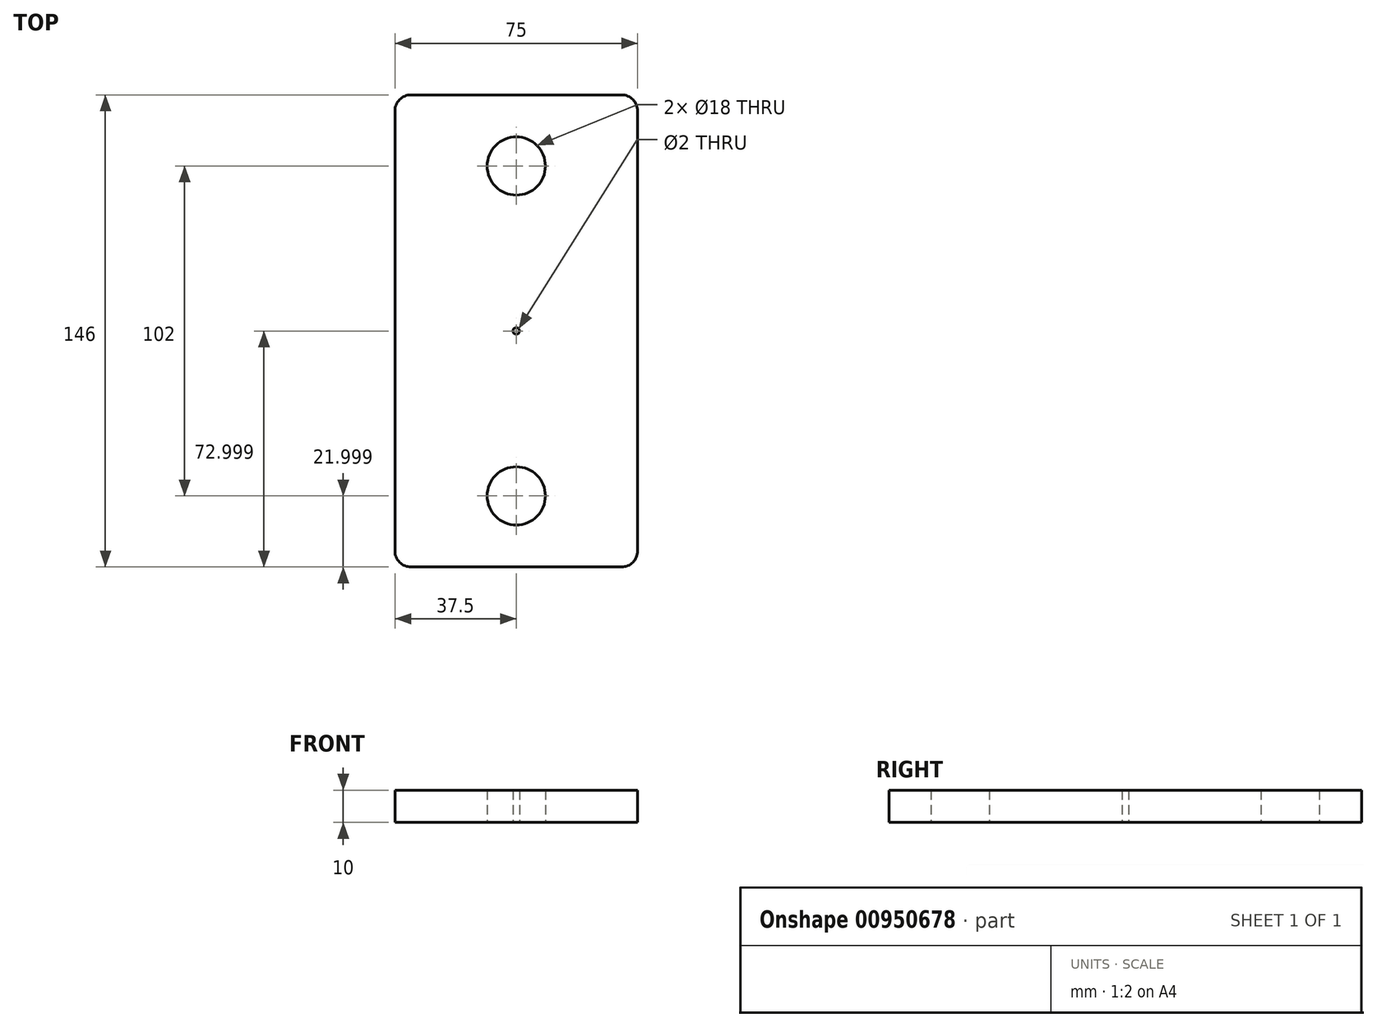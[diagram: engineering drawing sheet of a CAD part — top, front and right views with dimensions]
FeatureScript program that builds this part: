
annotation { "Feature Type Name" : "Feature", "Feature Type Description" : "" }
export const myFeature = defineFeature(function(context is Context, id is Id, definition is map)
    precondition{}
    {
        {
            var Q0;
            Q0=qCreatedBy(makeId("Top.planeOp"),FACE);
            var sketch = newSketch(context, id + "F0", { "sketchPlane" : qUnion([Q0])});
            skLineSegment(sketch, "E0.bottom", {"start": v(32.5, 71.97) * mm, "end": v(-32.5, 71.97) * mm});
            skLineSegment(sketch, "E0.top", {"start": v(32.5, -74.03) * mm, "end": v(-32.5, -74.03) * mm});
            skLineSegment(sketch, "E0.left", {"start": v(37.5, 66.97) * mm, "end": v(37.5, -69.03) * mm});
            skLineSegment(sketch, "E0.right", {"start": v(-37.5, 66.97) * mm, "end": v(-37.5, -69.03) * mm});
            skPoint(sketch, "E0.middle", {"position": v(0, -1.03) * mm});
            skLineSegment(sketch, "E1", {"start": v(0, -1.03) * mm, "end": v(0, -52.03) * mm});
            skLineSegment(sketch, "E2", {"start": v(0, -1.03) * mm, "end": v(0, 49.97) * mm});
            skCircle(sketch, "E3", {"center": v(0, 49.97) * mm, "radius": 9 * mm});
            skCircle(sketch, "E4", {"center": v(0, -52.03) * mm, "radius": 9 * mm});
            skCircle(sketch, "E5", {"center": v(0, -1.03) * mm, "radius": 1 * mm});
            skPoint(sketch, "E6.visualSharp", {"position": v(-37.5, 71.97) * mm});
            skArc(sketch, "E6.filletArc", {"start": v(-32.5, 71.97) * mm, "mid": v(-36.04, 70.5) * mm, "end": v(-37.5, 66.97) * mm});
            skPoint(sketch, "E7.visualSharp", {"position": v(37.5, 71.97) * mm});
            skArc(sketch, "E7.filletArc", {"start": v(37.5, 66.97) * mm, "mid": v(36.04, 70.5) * mm, "end": v(32.5, 71.97) * mm});
            skPoint(sketch, "E8.visualSharp", {"position": v(37.5, -74.03) * mm});
            skArc(sketch, "E8.filletArc", {"start": v(32.5, -74.03) * mm, "mid": v(36.04, -72.57) * mm, "end": v(37.5, -69.03) * mm});
            skPoint(sketch, "E9.visualSharp", {"position": v(-37.5, -74.03) * mm});
            skArc(sketch, "E9.filletArc", {"start": v(-37.5, -69.03) * mm, "mid": v(-36.04, -72.57) * mm, "end": v(-32.5, -74.03) * mm});
            skSolve(sketch);
        }
        {
            var Q0;
            Q0=makeQuery(id+"F0.imprint","IMPRINT",FACE,{"disambiguationData":[TD([[makeQuery(id+"F0.imprint","IMPRINT",EDGE,{"derivedFrom":sQuery(id+"F0.wireOp",EDGE,"E0.bottom")}),1.0]])]});
            extrude(context, id + "F1", {"entities" : qUnion([Q0]), "depth" : 10 * mm, "offsetDistance" : 25 * mm});
        }
    });
